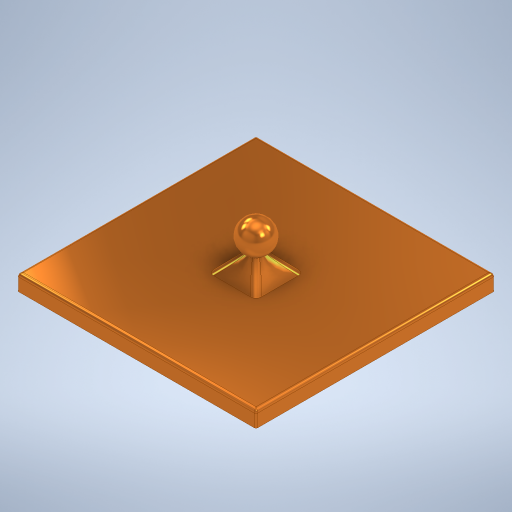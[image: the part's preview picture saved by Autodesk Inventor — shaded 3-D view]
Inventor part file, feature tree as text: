
AUTODESK INVENTOR PART (.ipt)
format: ipt  version: 2023 (Build 270158000, 158)  size: 387,584 bytes
history: native  units: mm
features: sketch x5, fillet x3, extrude x2, plane x2, revolve x1, loft x1, chamfer x1
ambient origin geometry x8: Origin, YZ Plane, XZ Plane, XY Plane, X Axis, Y Axis, Z Axis, Center Point
bodies: Solid1 (feature_tree)
feature tree (15):
  extrude  "Extrusion1"  Depth=150.0mm
  plane  "Work Plane1"
  revolve  "Revolution1"  [1 undecoded]
  sketch  "Sketch6"  dims[d4=10.0mm d5=0.0mm d6=20.0mm d7=20.0mm]
  plane  "Work Plane2"
  loft  "Loft1"
  fillet  "Fillet1"  Radius=20.0mm
  extrude  "Extrusion2"  TaperAngle=90.0deg  [1 undecoded]
  fillet  "Fillet2"  Radius=30.0mm
  fillet  "Fillet3"  Radius=30.0mm
  chamfer  "Chamfer1"  Distance=8.0mm
  sketch  "Sketch1"  dims[d0=150.0mm d1=150.0mm]
  sketch  "Sketch5"  dims[d2=75.0mm d3=75.0mm]
  sketch  "Sketch7"  dims[d8=10.0mm d9=90.0deg d10=30.0mm d11=30.0mm]
  sketch  "Sketch8"  dims[d13=-8.0mm d14=8.0mm d15=0.0mm d16=90.0deg d17=0.0mm d18=90.0deg d19=5.0mm d24=2.0mm d25=0.0mm d26=2.0mm d27=1.0mm d30=2.6mm d31=2.6mm d32=2.6mm d33=2.6mm d34=0.5mm d35=2.0mm d36=45.0deg]
note: 2 required parameter values undecoded (feature->parameter linkage not recoverable at this tier; creation-order binding heuristic only, values carry confidence <= 0.55)